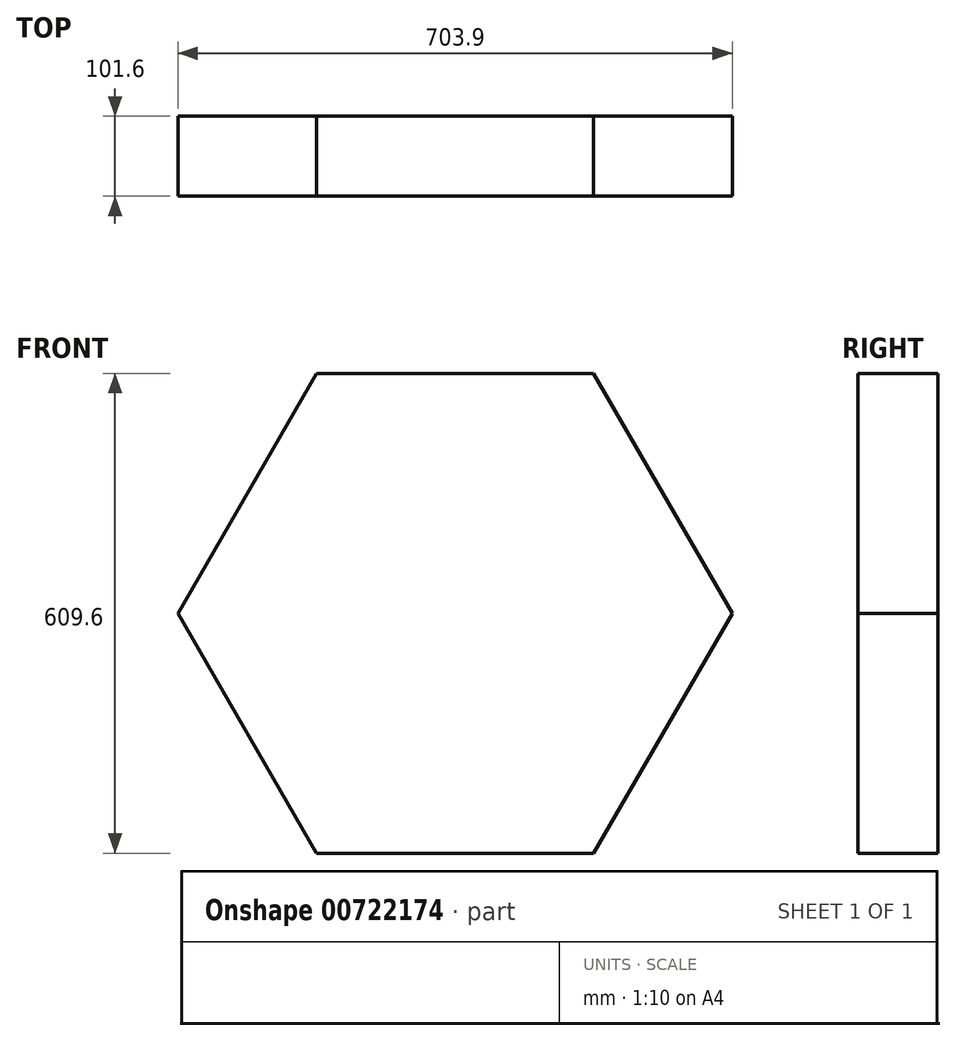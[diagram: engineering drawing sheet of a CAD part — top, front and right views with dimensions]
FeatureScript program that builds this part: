
annotation { "Feature Type Name" : "Feature", "Feature Type Description" : "" }
export const myFeature = defineFeature(function(context is Context, id is Id, definition is map)
    precondition{}
    {
        {
            var Q0;
            Q0=qCreatedBy(makeId("Front.planeOp"),FACE);
            var sketch = newSketch(context, id + "F0", { "sketchPlane" : qUnion([Q0])});
            skCircle(sketch, "E0.cCircle", {"center": v(0, 0) * mm, "radius": 304.8 * mm, "construction": true});
            skLineSegment(sketch, "E0.0", {"start": v(351.95, 0) * mm, "end": v(175.98, -304.8) * mm});
            skLineSegment(sketch, "E0.1", {"start": v(175.98, -304.8) * mm, "end": v(-175.98, -304.8) * mm});
            skLineSegment(sketch, "E0.2", {"start": v(-175.98, -304.8) * mm, "end": v(-351.95, 0) * mm});
            skLineSegment(sketch, "E0.3", {"start": v(-351.95, 0) * mm, "end": v(-175.98, 304.8) * mm});
            skLineSegment(sketch, "E0.4", {"start": v(-175.98, 304.8) * mm, "end": v(175.98, 304.8) * mm});
            skLineSegment(sketch, "E0.5", {"start": v(175.98, 304.8) * mm, "end": v(351.95, 0) * mm});
            skPoint(sketch, "E0.0.midPoint", {"position": v(263.96, -152.4) * mm});
            skSolve(sketch);
        }
        {
            var Q0;
            Q0=qSketchRegion(id+"F0",true);
            extrude(context, id + "F1", {"entities" : qUnion([Q0]), "depth" : 101.6 * mm, "offsetDistance" : 25.4 * mm});
        }
    });
